# Revit family: IEK_Кронштейн для мачты_500-800мм_Телескопический
name_source: partatom
category: Обобщенные модели
units: mm (PartAtom-declared; Revit-internal decimal feet)

## family parameters
Может служить основой для арматурных стержней = Нет
Общий = Да
Основа = Грань
При загрузке вырезать с полостями = Нет
Размер круглого соединителя = Использовать диаметр
Тип детали = Нормальный
Точка расчета площади = Нет

## types (1)
- 500-800мм
    ADSK_URL страницы изделия = https://www.iek.ru
    ADSK_Версия Revit = 2019
    ADSK_Версия семейства = 1.0
    ADSK_Группирование = VIII. ЭЛЕМЕНТЫ ВНЕШНЕЙ МОЛНИЕЗАЩИТЫ
    ADSK_Единица измерения = шт
    ADSK_Завод-изготовитель = IEK
    ADSK_Код изделия = ZML10D-MB-03-800
    ADSK_Масса = 3.6
    ADSK_Материал = Окраска - RAL 7035, светло-серый
    ADSK_Материал наименование = Сталь
    ADSK_Наименование = Кронштейн для мачты 500-800мм телескопический IEK
    IEK_URL = https://www.iek.ru
    IEK_Описание = Кронштейн для мачты 500 – 800 мм телескопический товарного знака IEK используется для закрепления мачты молниеприемной на фасаде здания или других вертикальных поверхностях. Для крепления изделия имеют фланец с отверстиями диаметром 12 мм.
    IEK_Цена за единицу = 4494
    KSI_CMa_Строительные материалы = 24.10.35.000.08.3.05.06-0001
    Отметка по умолчанию = 0 мм
